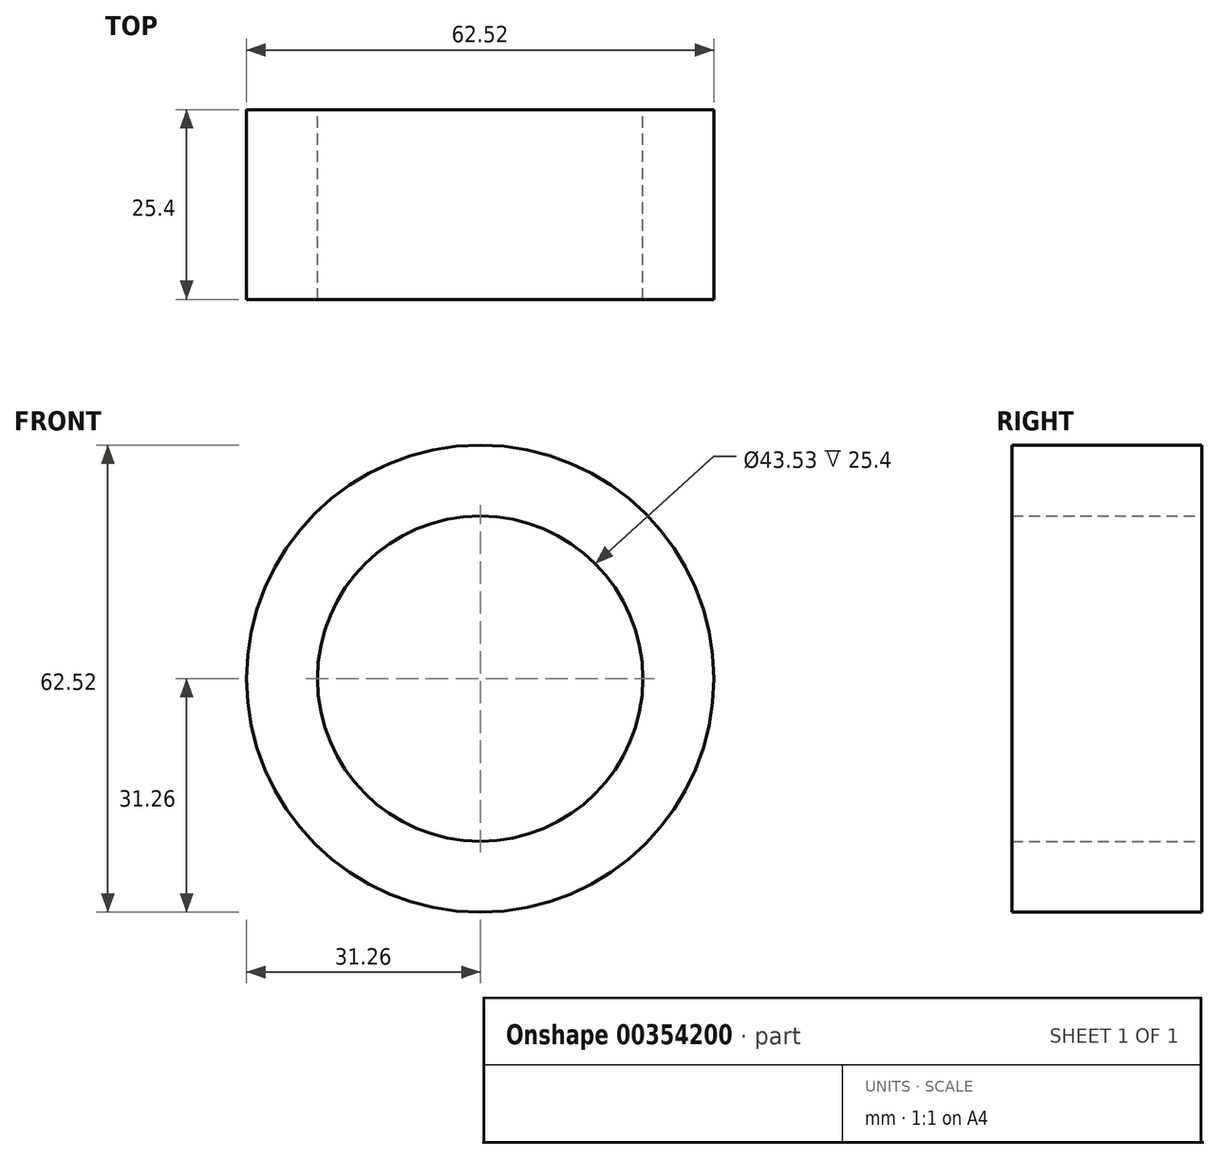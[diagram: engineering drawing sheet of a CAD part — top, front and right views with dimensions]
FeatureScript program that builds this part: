
annotation { "Feature Type Name" : "Feature", "Feature Type Description" : "" }
export const myFeature = defineFeature(function(context is Context, id is Id, definition is map)
    precondition{}
    {
        {
            var Q0;
            Q0=qCreatedBy(makeId("Front.planeOp"),FACE);
            var sketch = newSketch(context, id + "F0", { "sketchPlane" : qUnion([Q0])});
            skCircle(sketch, "E0", {"center": v(0, 0) * mm, "radius": 31.26 * mm});
            skCircle(sketch, "E1", {"center": v(0, 0) * mm, "radius": 21.77 * mm});
            skSolve(sketch);
        }
        {
            var Q0;
            Q0 = qSketchRegion(id + "F0", true);
            extrude(context, id + "F1", {"entities" : qUnion([Q0]), "depth" : 25.4 * mm});
        }
    });
